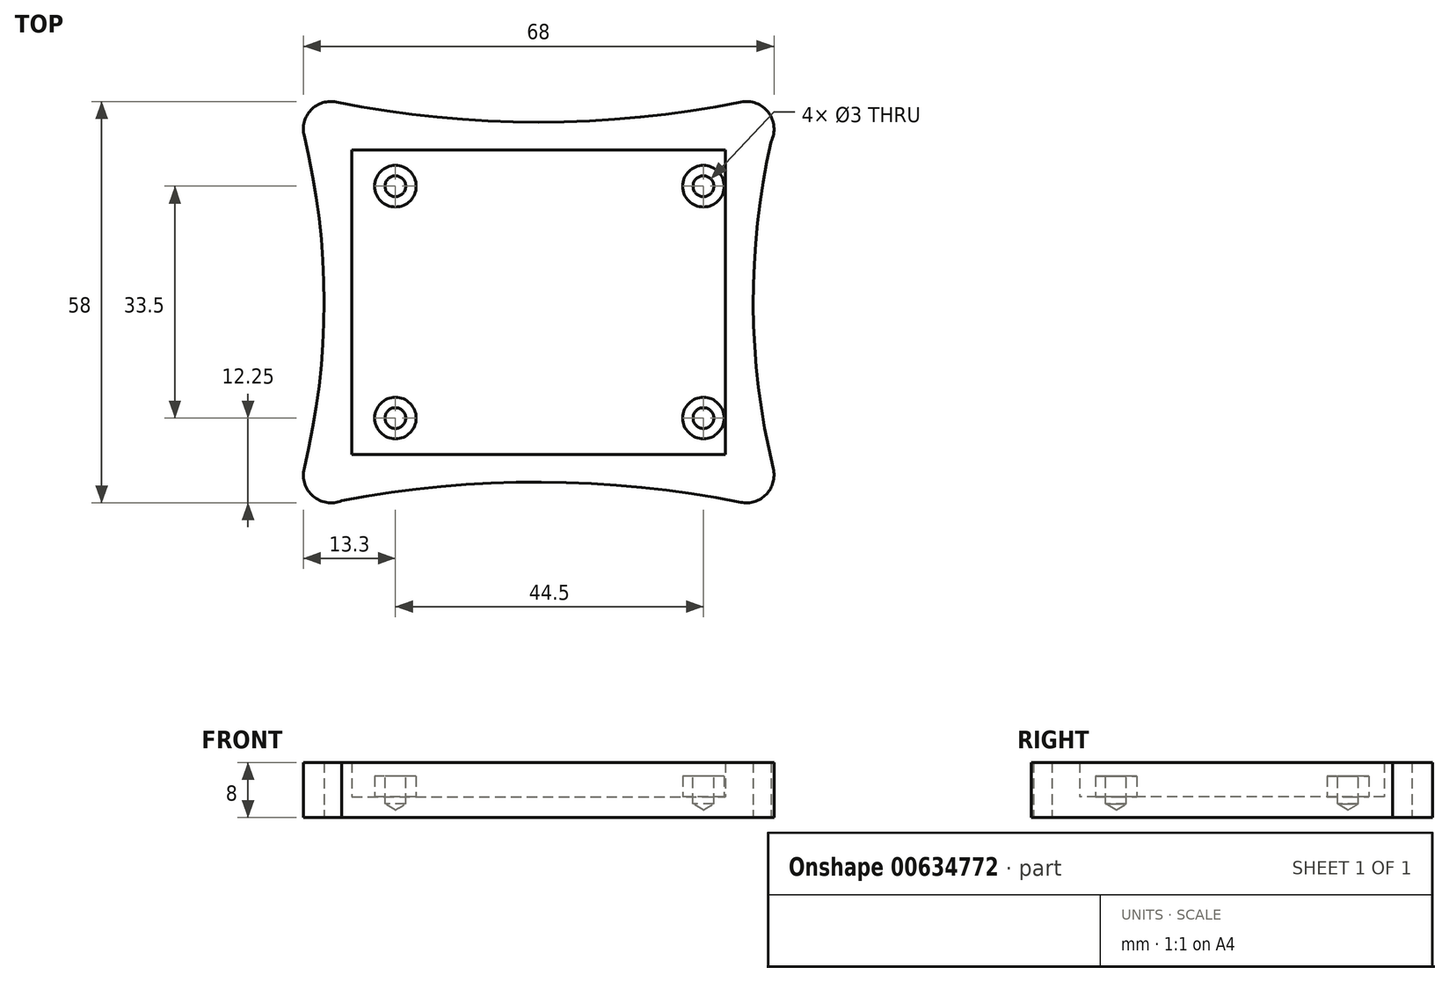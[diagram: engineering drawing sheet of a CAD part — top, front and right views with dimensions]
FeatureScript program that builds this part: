
annotation { "Feature Type Name" : "Feature", "Feature Type Description" : "" }
export const myFeature = defineFeature(function(context is Context, id is Id, definition is map)
    precondition{}
    {
        {
            var Q0;
            Q0=qCreatedBy(makeId("Top.planeOp"),FACE);
            var sketch = newSketch(context, id + "F0", { "sketchPlane" : qUnion([Q0])});
            skLineSegment(sketch, "E0.bottom", {"start": v(-30, 25) * mm, "end": v(30, 25) * mm});
            skLineSegment(sketch, "E0.top", {"start": v(-30, -25) * mm, "end": v(30, -25) * mm});
            skLineSegment(sketch, "E0.left", {"start": v(-30, 25) * mm, "end": v(-30, -25) * mm});
            skLineSegment(sketch, "E0.right", {"start": v(30, 25) * mm, "end": v(30, -25) * mm});
            skLineSegment(sketch, "E1", {"start": v(-30, 25) * mm, "end": v(30, -25) * mm, "construction": true});
            skSolve(sketch);
        }
        {
            var Q0;
            Q0=qSketchRegion(id+"F0",true);
            extrude(context, id + "F1", {"entities" : qUnion([Q0]), "depth" : 8 * mm, "offsetDistance" : 25 * mm});
        }
        {
            var Q0;
            Q0=makeQuery(id+"F1.opExtrude","CAP_FACE",FACE,{"disambiguationData":[OSD([sQuery(id+"F0.wireOp",EDGE,"E0.bottom"),sQuery(id+"F0.wireOp",EDGE,"E0.top"),sQuery(id+"F0.wireOp",EDGE,"E0.left"),sQuery(id+"F0.wireOp",EDGE,"E0.right")])],"isStart":false});
            shell(context, id + "F2", {"entities" : qUnion([Q0]), "thickness" : 3 * mm});
        }
        {
            var Q0;
            Q0=makeQuery(id+"F0.imprint","IMPRINT",FACE,{"disambiguationData":[TD([[makeQuery(id+"F0.imprint","IMPRINT",EDGE,{"derivedFrom":sQuery(id+"F0.wireOp",EDGE,"E0.bottom")}),-1.0]])]});
            var sketch = newSketch(context, id + "F3", { "sketchPlane" : qUnion([Q0])});
            skLineSegment(sketch, "E2.bottom", {"start": v(-20.7, 16.75) * mm, "end": v(23.8, 16.75) * mm, "construction": true});
            skLineSegment(sketch, "E2.top", {"start": v(-20.7, -16.75) * mm, "end": v(23.8, -16.75) * mm, "construction": true});
            skLineSegment(sketch, "E2.left", {"start": v(-20.7, 16.75) * mm, "end": v(-20.7, -16.75) * mm, "construction": true});
            skLineSegment(sketch, "E2.right", {"start": v(23.8, 16.75) * mm, "end": v(23.8, -16.75) * mm, "construction": true});
            skLineSegment(sketch, "E3", {"start": v(30, 0) * mm, "end": v(-30, 0) * mm, "construction": true});
            skLineSegment(sketch, "E4", {"start": v(-10.7, 0) * mm, "end": v(23.8, 0) * mm, "construction": true});
            skCircle(sketch, "E5.0", {"center": v(-20.7, 16.75) * mm, "radius": 3 * mm});
            skCircle(sketch, "E6.0", {"center": v(-20.7, -16.75) * mm, "radius": 3 * mm});
            skCircle(sketch, "E7.0", {"center": v(23.8, 16.75) * mm, "radius": 3 * mm});
            skCircle(sketch, "E8.0", {"center": v(23.8, -16.75) * mm, "radius": 3 * mm});
            skSolve(sketch);
        }
        {
            var Q0;
            Q0=makeQuery(id+"F3.imprint","IMPRINT",FACE,{"disambiguationData":[TD([[makeQuery(id+"F3.imprint","IMPRINT",EDGE,{"derivedFrom":sQuery(id+"F3.wireOp",EDGE,"E6.0")}),1.0]])]});
            var Q1;
            Q1=makeQuery(id+"F3.imprint","IMPRINT",FACE,{"disambiguationData":[TD([[makeQuery(id+"F3.imprint","IMPRINT",EDGE,{"derivedFrom":sQuery(id+"F3.wireOp",EDGE,"E5.0")}),1.0]])]});
            var Q2;
            Q2=makeQuery(id+"F3.imprint","IMPRINT",FACE,{"disambiguationData":[TD([[makeQuery(id+"F3.imprint","IMPRINT",EDGE,{"derivedFrom":sQuery(id+"F3.wireOp",EDGE,"E8.0")}),1.0]])]});
            var Q3;
            Q3=makeQuery(id+"F3.imprint","IMPRINT",FACE,{"disambiguationData":[TD([[makeQuery(id+"F3.imprint","IMPRINT",EDGE,{"derivedFrom":sQuery(id+"F3.wireOp",EDGE,"E7.0")}),1.0]])]});
            extrude(context, id + "F4", {"entities" : qUnion([Q0, Q1, Q2, Q3]), "operationType" : NewBodyOperationType.ADD, "depth" : 6 * mm, "offsetDistance" : 25 * mm});
        }
        {
            var Q0;
            Q0=makeQuery(id+"F4.opExtrude","CAP_FACE",FACE,{"disambiguationData":[OSD([sQuery(id+"F3.wireOp",EDGE,"E7.0")])],"isStart":false});
            var sketch = newSketch(context, id + "F5", { "sketchPlane" : qUnion([Q0])});
            skCircle(sketch, "E9", {"center": v(23.8, 16.75) * mm, "radius": 3 * mm});
            skCircle(sketch, "E10", {"center": v(-20.7, 16.75) * mm, "radius": 3 * mm});
            skCircle(sketch, "E11", {"center": v(23.8, -16.75) * mm, "radius": 3 * mm});
            skCircle(sketch, "E12", {"center": v(-20.7, -16.75) * mm, "radius": 3 * mm});
            skSolve(sketch);
        }
        {
            var Q0;
            Q0=sQuery(id+"F5.wireOp",VERTEX,"E9.center");
            var Q1;
            Q1=sQuery(id+"F5.wireOp",VERTEX,"E11.center");
            var Q2;
            Q2=sQuery(id+"F5.wireOp",VERTEX,"E12.center");
            var Q3;
            Q3=sQuery(id+"F5.wireOp",VERTEX,"E10.center");
            var Q4;
            Q4=makeQuery(id+"F1.opExtrude","SWEPT_BODY",BODY,{"disambiguationData":[OSD([sQuery(id+"F0.wireOp",EDGE,"E0.bottom"),sQuery(id+"F0.wireOp",EDGE,"E0.top"),sQuery(id+"F0.wireOp",EDGE,"E0.left"),sQuery(id+"F0.wireOp",EDGE,"E0.right")])]});
            hole(context, id + "F6", {"style" : HoleStyle.SIMPLE, "endStyle" : HoleEndStyle.BLIND, "holeDiameter" : 3 * mm, "majorDiameter" : 5 * mm, "holeDepth" : 4 * mm, "isTappedThrough" : true, "tappedDepth" : 12 * mm, "tapClearance" : 3, "locations" : qUnion([Q0, Q1, Q2, Q3]), "scope" : qUnion([Q4])});
        }
        {
            var Q0;
            Q0=makeQuery(id+"F3.imprint","IMPRINT",FACE,{"disambiguationData":[TD([[makeQuery(id+"F3.imprint","IMPRINT",EDGE,{"derivedFrom":sQuery(id+"F3.wireOp",EDGE,"E5.0")}),-1.0]])]});
            var sketch = newSketch(context, id + "F7", { "sketchPlane" : qUnion([Q0])});
            skArc(sketch, "E13", {"start": v(-29.2, 28.92) * mm, "mid": v(-32.88, 27.77) * mm, "end": v(-33.89, 24.05) * mm});
            skArc(sketch, "E14", {"start": v(-33.89, -24.05) * mm, "mid": v(-32.6, -28.04) * mm, "end": v(-28.48, -28.7) * mm});
            skArc(sketch, "E15", {"start": v(29.21, -28.92) * mm, "mid": v(32.89, -27.77) * mm, "end": v(33.89, -24.05) * mm});
            skArc(sketch, "E16", {"start": v(33.58, 23.2) * mm, "mid": v(33.18, 27.43) * mm, "end": v(29.2, 28.92) * mm});
            skArc(sketch, "E17", {"start": v(-33.89, -24.05) * mm, "mid": v(-31, 0.4) * mm, "end": v(-34.08, 24.82) * mm});
            skArc(sketch, "E18", {"start": v(-29.2, 28.92) * mm, "mid": v(0, 26) * mm, "end": v(29.2, 28.92) * mm});
            skArc(sketch, "E19", {"start": v(29.21, -28.92) * mm, "mid": v(-0.4, -26) * mm, "end": v(-30, -29) * mm});
            skArc(sketch, "E20", {"start": v(34, 25) * mm, "mid": v(31, 0.48) * mm, "end": v(33.89, -24.05) * mm});
            skLineSegment(sketch, "E21", {"start": v(30, 25) * mm, "end": v(-30, 25) * mm});
            skLineSegment(sketch, "E22", {"start": v(-30, -25) * mm, "end": v(-30, 25) * mm});
            skLineSegment(sketch, "E23", {"start": v(-30, -25) * mm, "end": v(30, -25) * mm});
            skLineSegment(sketch, "E24", {"start": v(30, -25) * mm, "end": v(30, 25) * mm});
            skSolve(sketch);
        }
        {
            var Q0;
            Q0 = qSketchRegion(id + "F7", true);
            var Q1;
            Q1=makeQuery(id+"F1.opExtrude","CAP_FACE",FACE,{"disambiguationData":[OSD([sQuery(id+"F0.wireOp",EDGE,"E0.bottom"),sQuery(id+"F0.wireOp",EDGE,"E0.top"),sQuery(id+"F0.wireOp",EDGE,"E0.left"),sQuery(id+"F0.wireOp",EDGE,"E0.right")])],"isStart":false});
            extrude(context, id + "F8", {"entities" : qUnion([Q0]), "operationType" : NewBodyOperationType.ADD, "endBound" : BoundingType.UP_TO_SURFACE, "depth" : 25 * mm, "endBoundEntityFace" : qUnion([Q1]), "offsetDistance" : 25 * mm});
        }
    });
